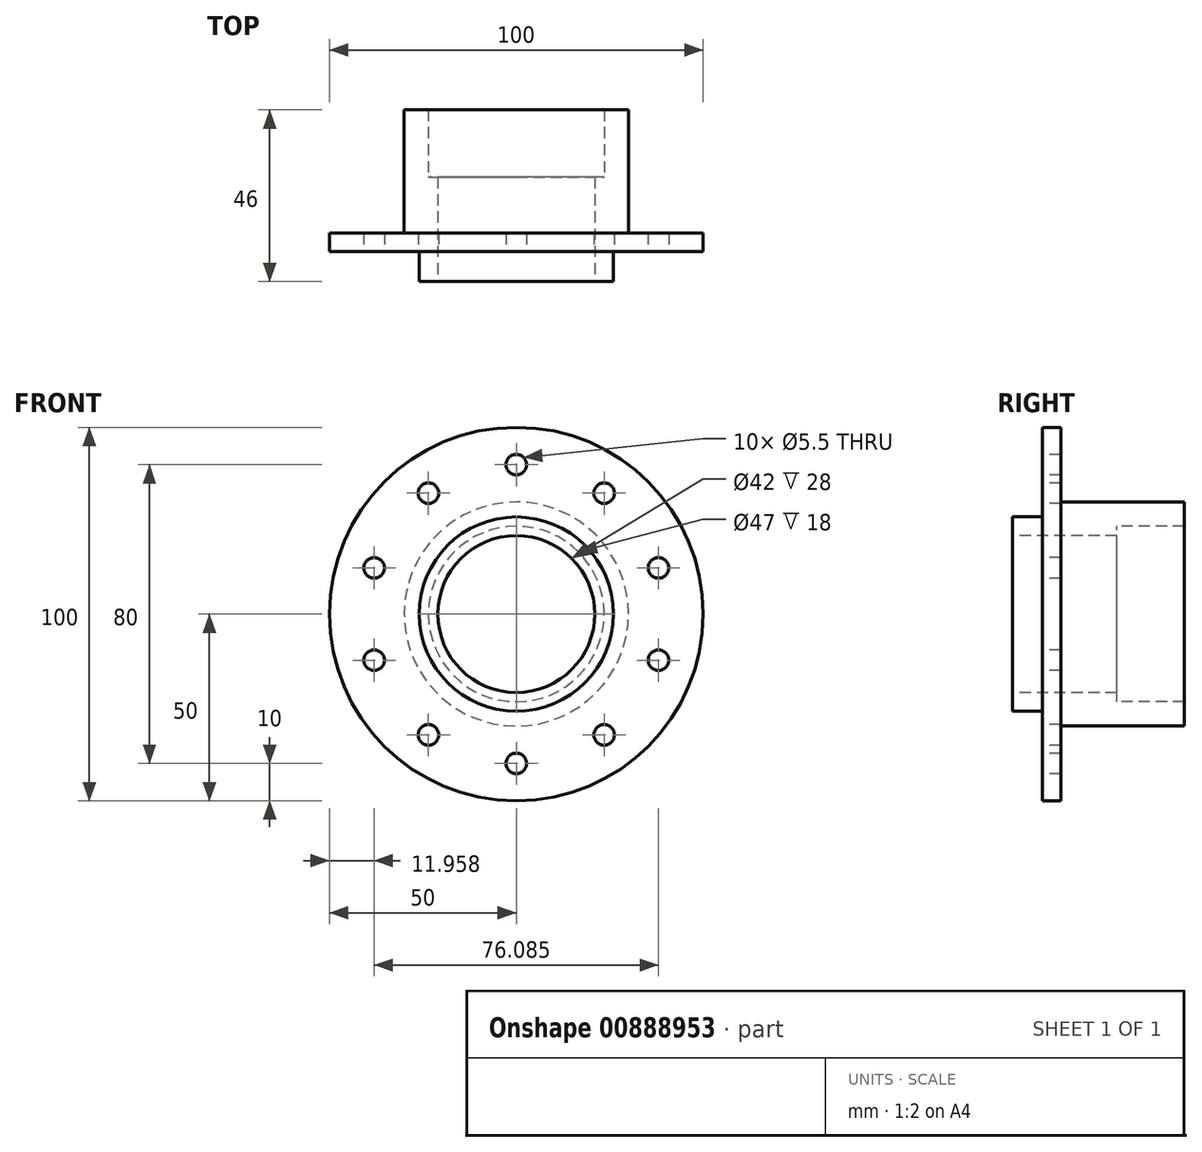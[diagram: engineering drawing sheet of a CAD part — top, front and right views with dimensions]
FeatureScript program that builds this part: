
annotation { "Feature Type Name" : "Feature", "Feature Type Description" : "" }
export const myFeature = defineFeature(function(context is Context, id is Id, definition is map)
    precondition{}
    {
        {
            var Q0;
            Q0=qCreatedBy(makeId("Right.planeOp"),FACE);
            var sketch = newSketch(context, id + "F0", { "sketchPlane" : qUnion([Q0])});
            skLineSegment(sketch, "E0", {"start": v(46, 9) * mm, "end": v(13, 9) * mm});
            skLineSegment(sketch, "E1", {"start": v(13, 9) * mm, "end": v(13, 29) * mm});
            skLineSegment(sketch, "E2", {"start": v(13, 29) * mm, "end": v(8, 29) * mm});
            skLineSegment(sketch, "E3", {"start": v(8, 29) * mm, "end": v(8, 5) * mm});
            skLineSegment(sketch, "E4", {"start": v(8, 5) * mm, "end": v(0, 5) * mm});
            skLineSegment(sketch, "E5", {"start": v(0, 5) * mm, "end": v(0, 0) * mm});
            skLineSegment(sketch, "E6", {"start": v(0, 0) * mm, "end": v(28, 0) * mm});
            skLineSegment(sketch, "E7", {"start": v(28, 0) * mm, "end": v(28, 2.5) * mm});
            skLineSegment(sketch, "E8", {"start": v(28, 2.5) * mm, "end": v(46, 2.5) * mm});
            skLineSegment(sketch, "E9", {"start": v(46, 2.5) * mm, "end": v(46, 9) * mm});
            skLineSegment(sketch, "E10", {"start": v(-6.72, -21) * mm, "end": v(58.83, -21) * mm, "construction": true});
            skSolve(sketch);
        }
        {
            var Q0;
            Q0=makeQuery(id+"F0.imprint","IMPRINT",FACE,{"disambiguationData":[TD([[makeQuery(id+"F0.imprint","IMPRINT",EDGE,{"derivedFrom":sQuery(id+"F0.wireOp",EDGE,"E0")}),1.0]])]});
            var Q1;
            Q1=sQuery(id+"F0.wireOp",EDGE,"E10");
            revolve(context, id + "F1", {"surfaceOperationType" : NewSurfaceOperationType.NEW, "entities" : qUnion([Q0]), "axis" : qUnion([Q1]), "revolveType" : RevolveType.FULL});
        }
        {
            var Q0;
            Q0=makeQuery(id+"F1.opRevolve","SWEPT_FACE",FACE,{"disambiguationData":[OSD([sQuery(id+"F0.wireOp",EDGE,"E3")])]});
            var sketch = newSketch(context, id + "F2", { "sketchPlane" : qUnion([Q0])});
            skCircle(sketch, "E11", {"center": v(0, -21) * mm, "radius": 40 * mm, "construction": true});
            skCircle(sketch, "E12", {"center": v(0, 19) * mm, "radius": 2.75 * mm});
            skLineSegment(sketch, "E13", {"start": v(0, 29) * mm, "end": v(0, -40.43) * mm, "construction": true});
            skCircle(sketch, "E14.1.0", {"center": v(-23.51, 11.36) * mm, "radius": 2.75 * mm});
            skCircle(sketch, "E14.2.0", {"center": v(-38.04, -8.64) * mm, "radius": 2.75 * mm});
            skCircle(sketch, "E14.3.0", {"center": v(-38.04, -33.36) * mm, "radius": 2.75 * mm});
            skCircle(sketch, "E14.4.0", {"center": v(-23.51, -53.36) * mm, "radius": 2.75 * mm});
            skCircle(sketch, "E14.5.0", {"center": v(0, -61) * mm, "radius": 2.75 * mm});
            skCircle(sketch, "E14.6.0", {"center": v(23.51, -53.36) * mm, "radius": 2.75 * mm});
            skCircle(sketch, "E14.7.0", {"center": v(38.04, -33.36) * mm, "radius": 2.75 * mm});
            skCircle(sketch, "E14.8.0", {"center": v(38.04, -8.64) * mm, "radius": 2.75 * mm});
            skCircle(sketch, "E14.9.0", {"center": v(23.51, 11.36) * mm, "radius": 2.75 * mm});
            skSolve(sketch);
        }
        {
            var Q0;
            Q0=makeQuery(id+"F2.imprint","IMPRINT",FACE,{"disambiguationData":[TD([[makeQuery(id+"F2.imprint","IMPRINT",EDGE,{"derivedFrom":sQuery(id+"F2.wireOp",EDGE,"E14.1.0")}),1.0]])]});
            var Q1;
            Q1=makeQuery(id+"F2.imprint","IMPRINT",FACE,{"disambiguationData":[TD([[makeQuery(id+"F2.imprint","IMPRINT",EDGE,{"derivedFrom":sQuery(id+"F2.wireOp",EDGE,"E14.2.0")}),1.0]])]});
            var Q2;
            Q2=makeQuery(id+"F2.imprint","IMPRINT",FACE,{"disambiguationData":[TD([[makeQuery(id+"F2.imprint","IMPRINT",EDGE,{"derivedFrom":sQuery(id+"F2.wireOp",EDGE,"E14.3.0")}),1.0]])]});
            var Q3;
            Q3=makeQuery(id+"F2.imprint","IMPRINT",FACE,{"disambiguationData":[TD([[makeQuery(id+"F2.imprint","IMPRINT",EDGE,{"derivedFrom":sQuery(id+"F2.wireOp",EDGE,"E14.4.0")}),1.0]])]});
            var Q4;
            Q4=makeQuery(id+"F2.imprint","IMPRINT",FACE,{"disambiguationData":[TD([[makeQuery(id+"F2.imprint","IMPRINT",EDGE,{"derivedFrom":sQuery(id+"F2.wireOp",EDGE,"E14.5.0")}),1.0]])]});
            var Q5;
            Q5=makeQuery(id+"F2.imprint","IMPRINT",FACE,{"disambiguationData":[TD([[makeQuery(id+"F2.imprint","IMPRINT",EDGE,{"derivedFrom":sQuery(id+"F2.wireOp",EDGE,"E14.6.0")}),1.0]])]});
            var Q6;
            Q6=makeQuery(id+"F2.imprint","IMPRINT",FACE,{"disambiguationData":[TD([[makeQuery(id+"F2.imprint","IMPRINT",EDGE,{"derivedFrom":sQuery(id+"F2.wireOp",EDGE,"E14.7.0")}),1.0]])]});
            var Q7;
            Q7=makeQuery(id+"F2.imprint","IMPRINT",FACE,{"disambiguationData":[TD([[makeQuery(id+"F2.imprint","IMPRINT",EDGE,{"derivedFrom":sQuery(id+"F2.wireOp",EDGE,"E14.8.0")}),1.0]])]});
            var Q8;
            Q8=makeQuery(id+"F2.imprint","IMPRINT",FACE,{"disambiguationData":[TD([[makeQuery(id+"F2.imprint","IMPRINT",EDGE,{"derivedFrom":sQuery(id+"F2.wireOp",EDGE,"E14.9.0")}),1.0]])]});
            var Q9;
            Q9=makeQuery(id+"F2.imprint","IMPRINT",FACE,{"disambiguationData":[TD([[makeQuery(id+"F2.imprint","IMPRINT",EDGE,{"derivedFrom":sQuery(id+"F2.wireOp",EDGE,"E12")}),1.0]])]});
            var Q10;
            Q10=sQuery(id+"F2.wireOp",EDGE,"E12");
            extrude(context, id + "F3", {"entities" : qUnion([Q0, Q1, Q2, Q3, Q4, Q5, Q6, Q7, Q8, Q9]), "operationType" : NewBodyOperationType.REMOVE, "surfaceEntities" : qUnion([Q10]), "oppositeDirection" : true, "depth" : 25 * mm, "offsetDistance" : 25 * mm});
        }
    });
